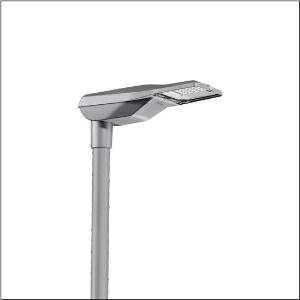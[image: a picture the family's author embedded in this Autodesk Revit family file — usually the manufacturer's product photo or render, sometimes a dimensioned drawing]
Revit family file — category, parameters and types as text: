
# Revit family: streetlight_sl_21_iq_micro___st0_8a_5xe1c41g08db_305a
name_source: partatom
category: Lighting Fixtures
units: mm (PartAtom-declared; Revit-internal decimal feet)

## family parameters
Cut with Voids When Loaded = No
Host = Face
Light Source = No
Part Type = Normal
Room Calculation Point = No
Round Connector Dimension = Use Diameter
Shared = No

## types (1)
- --- (1 x LED, 5010 lm, 36.4 W, 4000K)
    Apparent Load = 36 VA
    CIE Flux Codes = 38 75 97 100 100
    Color Rendering = 70
    Color Temperature = 4000K
    Default Elevation = 1800 mm
    Description = Streetlight SL 21 iQ micro, mast luminaire, primary light control with lens, of PMMA, primary optical cover: cover, of toughened safety glass, transparent, light distribution: ST0.8a, light emission: direct distribution, primary light characteristic: asymmetric, installation type: post-top, side-entry, LED, High Power LED, rated luminous flux: 5.010lm, luminous efficacy: 138lm/W, light colour: 740, colour temperature: 4000K, control: Street-Remote, Auto-Match, Temp-Guard, Lumen-Switch, Night-Set, Smart-Wire, Light-Fading, Desk-Remote (wireless, voltage-free reading and setting of iQ features in the workshop via application-optimized NFC function/RFID function), optimised constant luminous flux control (CLO 2.0), presetting dimming linear, mains connection: 220..240V, AC, 50/60Hz, start of lifetime: 36W, end of service life: 38W, reduction: 16W, luminaire housing, of diecast aluminium, powder-coated, Siteco® metallic grey (DB 702S), corrosivity category C5 mid according to DIN EN ISO 12944, please order mast flange separately, inclination adjustable: 0°, 5°, 10°, 15°, sealing non-destructively replaceable, multi-level sealing system, length: 528mm, width: 235mm, height: 110mm, mast flange for spigot size: 42mm (side-entry): 5XC10008XM4, 60/48mm (side-entry/post-top): 5XC10108XM2, 76/60mm (side-entry/post-top): 5XC10108XM1, protection rating (complete): IP66, insulation class (complete): insulation class II (safety insulation), certification: CE, ENEC, ENEC+, VDE, impact resistance: IK09, permissible operating ambient temperature for outdoor applications: -40..+50°C, standard-compliant lighting for roads and squares, packaging unit: 1 piece

Light Distribution: ST0.8a
    Height = 110 mm
    Lamp = 1 x LED
    Lamp Light Flux = 5010 lm
    Lamp Power = 36.4 W
    Lamp count = 1
    Length = 528 mm
    Luminous efficacy = 138 lm/W
    Manufacturer = Siteco
    ModVariant = No
    Model = 5XE1C41G08DB
    Number of Poles = 1
    OnlyDefault = Yes
    Power Factor = 1
    Product Name = Streetlight SL 21 iQ micro | ST0.8a
    Product group = mast luminaire | pylon top
    ProductGroupID = 6100
    Protection Class = Protection class II
    Protection Degree = IP 66
    RLX_Detail_Level = 1
    RLX_Emergency_Light_Flux = 0 lm
    RLX_Emergency_Type = 0
    RLX_Emergency_Type_DB = No
    RlxData = <blob elided: 98829 chars, md5=7ffc261a>
    Socket = socket
    Standby Power = 0 W
    System Light Flux = 5010 lm
    System Power = 36 W
    Type Comments = factory setting: luminous flux: 100 % | dim-lin: 254 | 715 mA
    Type Image = l_1006881.jpg
    URL = http://relux.com
    VarID = @adj_086769
    Voltage = 0 V
    Weight = 0.00 kg
    Width = 235 mm

## geometry (parser evidence)
native form markers: Blend x4, Sweep x9
no freeform markers — native parametric forms only
